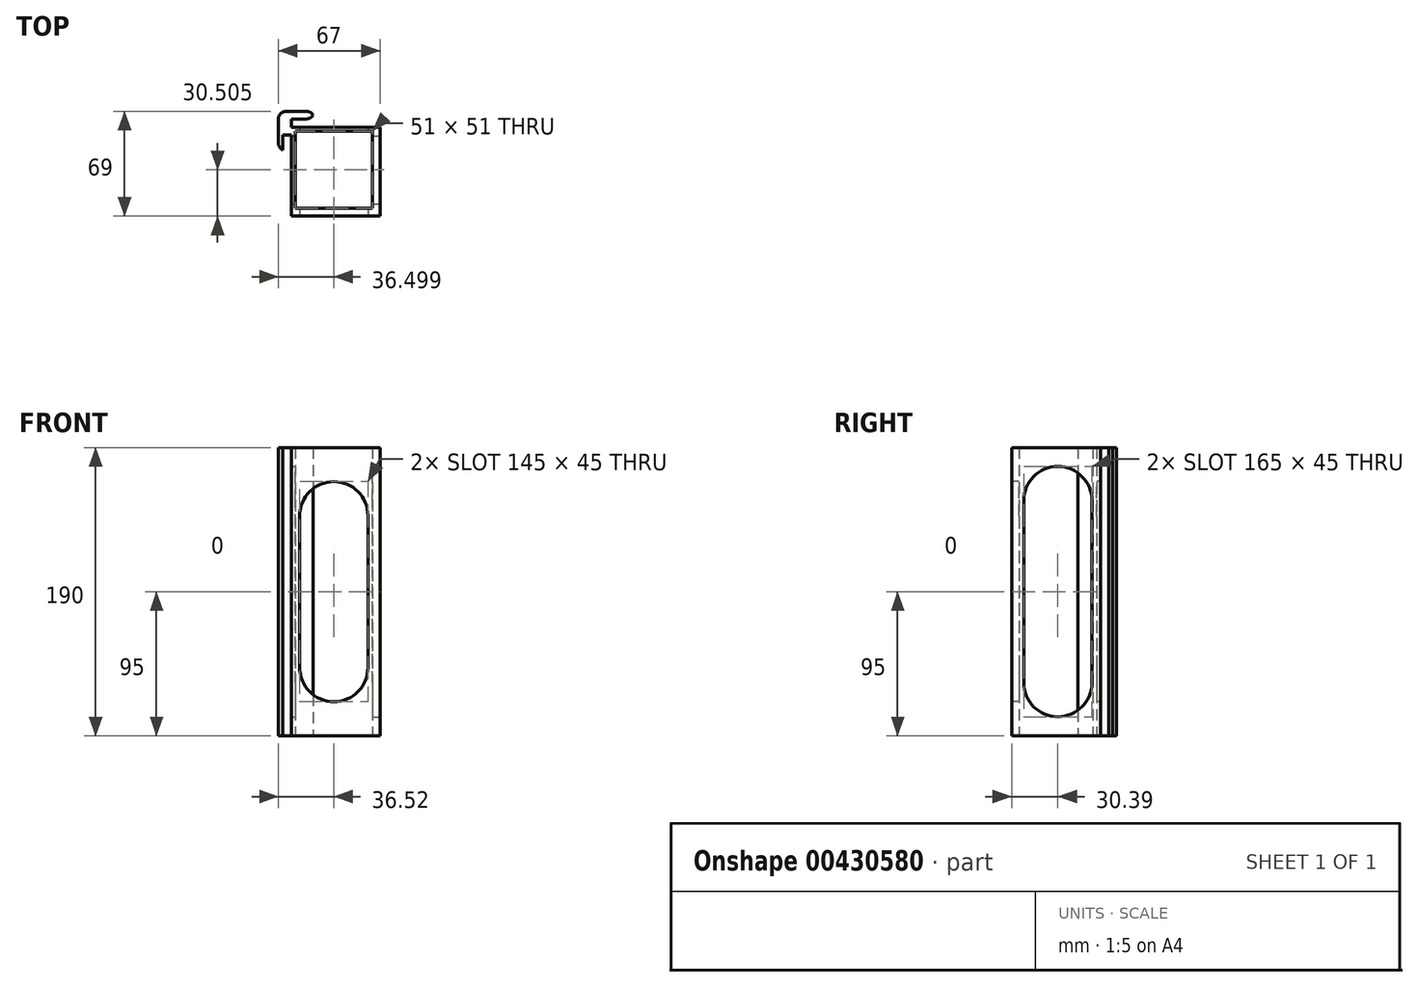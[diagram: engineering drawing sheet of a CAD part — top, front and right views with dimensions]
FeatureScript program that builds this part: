
annotation { "Feature Type Name" : "Feature", "Feature Type Description" : "" }
export const myFeature = defineFeature(function(context is Context, id is Id, definition is map)
    precondition{}
    {
        {
            var Q0;
            Q0=qCreatedBy(makeId("Top.planeOp"),FACE);
            var sketch = newSketch(context, id + "F0", { "sketchPlane" : qUnion([Q0])});
            skLineSegment(sketch, "E0.bottom", {"start": v(25.48, -25.39) * mm, "end": v(-25.52, -25.39) * mm});
            skLineSegment(sketch, "E0.top", {"start": v(25.48, 25.61) * mm, "end": v(-25.52, 25.61) * mm});
            skLineSegment(sketch, "E0.left", {"start": v(25.48, -25.39) * mm, "end": v(25.48, 25.61) * mm});
            skLineSegment(sketch, "E0.right", {"start": v(-25.52, -25.39) * mm, "end": v(-25.52, 25.61) * mm});
            skPoint(sketch, "E0.middle", {"position": v(-0.02, 0.11) * mm});
            skLineSegment(sketch, "E1.bottom", {"start": v(-28.02, 28.11) * mm, "end": v(30.48, 28.11) * mm});
            skLineSegment(sketch, "E1.top", {"start": v(-28.02, -30.39) * mm, "end": v(30.48, -30.39) * mm});
            skLineSegment(sketch, "E1.left", {"start": v(-28.02, 28.11) * mm, "end": v(-28.02, -30.39) * mm});
            skLineSegment(sketch, "E1.right", {"start": v(30.48, 28.11) * mm, "end": v(30.48, -30.39) * mm});
            skLineSegment(sketch, "E2.bottom", {"start": v(-28.02, 28.11) * mm, "end": v(-23.02, 28.11) * mm});
            skLineSegment(sketch, "E2.top", {"start": v(-28.02, 33.61) * mm, "end": v(-23.02, 33.61) * mm});
            skLineSegment(sketch, "E2.left", {"start": v(-28.02, 28.11) * mm, "end": v(-28.02, 33.61) * mm});
            skLineSegment(sketch, "E3.bottom", {"start": v(-28.02, 28.11) * mm, "end": v(-33.52, 28.11) * mm});
            skLineSegment(sketch, "E3.top", {"start": v(-28.02, 23.11) * mm, "end": v(-33.52, 23.11) * mm});
            skLineSegment(sketch, "E3.left", {"start": v(-28.02, 28.11) * mm, "end": v(-28.02, 23.11) * mm});
            skLineSegment(sketch, "E3.right", {"start": v(-33.52, 28.11) * mm, "end": v(-33.52, 23.11) * mm});
            skLineSegment(sketch, "E4.bottom", {"start": v(-33.52, 28.11) * mm, "end": v(-36.52, 28.11) * mm});
            skLineSegment(sketch, "E4.top", {"start": v(-33.52, 13.11) * mm, "end": v(-36.52, 13.11) * mm});
            skLineSegment(sketch, "E4.left", {"start": v(-33.52, 28.11) * mm, "end": v(-33.52, 13.11) * mm});
            skLineSegment(sketch, "E4.right", {"start": v(-36.52, 28.11) * mm, "end": v(-36.52, 13.11) * mm});
            skLineSegment(sketch, "E5.bottom", {"start": v(-28.02, 33.61) * mm, "end": v(-13.02, 33.61) * mm});
            skLineSegment(sketch, "E5.top", {"start": v(-28.02, 38.61) * mm, "end": v(-13.02, 38.61) * mm});
            skLineSegment(sketch, "E5.left", {"start": v(-28.02, 33.61) * mm, "end": v(-28.02, 38.61) * mm});
            skLineSegment(sketch, "E5.right", {"start": v(-13.02, 33.61) * mm, "end": v(-13.02, 38.61) * mm});
            skLineSegment(sketch, "E6.bottom", {"start": v(-28.02, 28.11) * mm, "end": v(-36.52, 28.11) * mm});
            skLineSegment(sketch, "E6.top", {"start": v(-28.02, 38.61) * mm, "end": v(-36.52, 38.61) * mm});
            skLineSegment(sketch, "E6.left", {"start": v(-28.02, 28.11) * mm, "end": v(-28.02, 38.61) * mm});
            skLineSegment(sketch, "E6.right", {"start": v(-36.52, 28.11) * mm, "end": v(-36.52, 38.61) * mm});
            skSolve(sketch);
        }
        {
            var Q0;
            {var subQ4=sQuery(id+"F0.wireOp",EDGE,"E6.top");Q0=makeQuery(id+"F0.imprint","IMPRINT",FACE,{"disambiguationData":[TD([[makeQuery(id+"F0.imprint","IMPRINT",EDGE,{"derivedFrom":subQ4}),1.0]])]});}
            var Q1;
            {var subQ4=sQuery(id+"F0.wireOp",EDGE,"E5.top");Q1=makeQuery(id+"F0.imprint","IMPRINT",FACE,{"disambiguationData":[TD([[makeQuery(id+"F0.imprint","IMPRINT",EDGE,{"derivedFrom":subQ4}),-1.0]])]});}
            var Q2;
            {var subQ0=sQuery(id+"F0.wireOp",EDGE,"E3.top");Q2=makeQuery(id+"F0.imprint","IMPRINT",FACE,{"disambiguationData":[TD([[makeQuery(id+"F0.imprint","IMPRINT",EDGE,{"derivedFrom":subQ0}),-1.0]])]});}
            var Q3;
            {var subQ3=sQuery(id+"F0.wireOp",EDGE,"E4.top");Q3=makeQuery(id+"F0.imprint","IMPRINT",FACE,{"disambiguationData":[TD([[makeQuery(id+"F0.imprint","IMPRINT",EDGE,{"derivedFrom":subQ3}),-1.0]])]});}
            var Q4;
            Q4=makeQuery(id+"F0.imprint","IMPRINT",FACE,{"disambiguationData":[TD([[makeQuery(id+"F0.imprint","IMPRINT",EDGE,{"derivedFrom":sQuery(id+"F0.wireOp",EDGE,"E0.bottom")}),1.0]])]});
            extrude(context, id + "F1", {"entities" : qUnion([Q0, Q1, Q2, Q3, Q4]), "depth" : 190 * mm, "offsetDistance" : 25 * mm});
        }
        {
            var Q0;
            Q0=makeQuery(id+"F1.opExtrude","SWEPT_EDGE",EDGE,{"disambiguationData":[OSD([sQuery(id+"F0.wireOp",EDGE,"E6.top"),sQuery(id+"F0.wireOp",EDGE,"E6.right")])]});
            var Q1;
            Q1=makeQuery(id+"F1.opExtrude","SWEPT_EDGE",EDGE,{"disambiguationData":[OSD([sQuery(id+"F0.wireOp",EDGE,"E5.top"),sQuery(id+"F0.wireOp",EDGE,"E5.right")])]});
            var Q2;
            Q2=makeQuery(id+"F1.opExtrude","SWEPT_EDGE",EDGE,{"disambiguationData":[OSD([sQuery(id+"F0.wireOp",EDGE,"E5.bottom"),sQuery(id+"F0.wireOp",EDGE,"E5.right")])]});
            var Q3;
            Q3=makeQuery(id+"F1.opExtrude","SWEPT_EDGE",EDGE,{"disambiguationData":[OSD([sQuery(id+"F0.wireOp",EDGE,"E4.top"),sQuery(id+"F0.wireOp",EDGE,"E4.right")])]});
            fillet(context, id + "F2", {"entities" : qUnion([Q0, Q1, Q2, Q3]), "tangentPropagation" : true, "radius" : 5 * mm, "defaultsChanged" : false, "vertexSettings" : [], "allowEdgeOverflow" : false});
        }
        {
            var Q0;
            Q0=makeQuery(id+"F1.opExtrude","SWEPT_FACE",FACE,{"disambiguationData":[OSD([sQuery(id+"F0.wireOp",EDGE,"E1.right")])]});
            var sketch = newSketch(context, id + "F3", { "sketchPlane" : qUnion([Q0])});
            skCircle(sketch, "E7", {"center": v(0, 35) * mm, "radius": 22.5 * mm});
            skCircle(sketch, "E8", {"center": v(0, 155) * mm, "radius": 22.5 * mm});
            skLineSegment(sketch, "E9.bottom", {"start": v(-22.5, 155) * mm, "end": v(22.5, 155) * mm});
            skLineSegment(sketch, "E9.top", {"start": v(-22.5, 35) * mm, "end": v(22.5, 35) * mm});
            skLineSegment(sketch, "E9.left", {"start": v(-22.5, 155) * mm, "end": v(-22.5, 35) * mm});
            skLineSegment(sketch, "E9.right", {"start": v(22.5, 155) * mm, "end": v(22.5, 35) * mm});
            skSolve(sketch);
        }
        {
            var Q0;
            {var subQ0=sQuery(id+"F3.wireOp",EDGE,"E9.bottom");Q0=makeQuery(id+"F3.imprint","IMPRINT",FACE,{"disambiguationData":[TD([[makeQuery(id+"F3.imprint","IMPRINT",EDGE,{"derivedFrom":subQ0}),1.0]])]});}
            var Q1;
            {var subQ0=sQuery(id+"F3.wireOp",EDGE,"E9.bottom");Q1=makeQuery(id+"F3.imprint","IMPRINT",FACE,{"disambiguationData":[TD([[makeQuery(id+"F3.imprint","IMPRINT",EDGE,{"derivedFrom":subQ0}),-1.0]])]});}
            var Q2;
            {var subQ0=sQuery(id+"F3.wireOp",EDGE,"E9.left");Q2=makeQuery(id+"F3.imprint","IMPRINT",FACE,{"disambiguationData":[TD([[makeQuery(id+"F3.imprint","IMPRINT",EDGE,{"derivedFrom":subQ0}),1.0]])]});}
            var Q3;
            {var subQ0=sQuery(id+"F3.wireOp",EDGE,"E9.top");Q3=makeQuery(id+"F3.imprint","IMPRINT",FACE,{"disambiguationData":[TD([[makeQuery(id+"F3.imprint","IMPRINT",EDGE,{"derivedFrom":subQ0}),1.0]])]});}
            var Q4;
            {var subQ0=sQuery(id+"F3.wireOp",EDGE,"E9.top");Q4=makeQuery(id+"F3.imprint","IMPRINT",FACE,{"disambiguationData":[TD([[makeQuery(id+"F3.imprint","IMPRINT",EDGE,{"derivedFrom":subQ0}),-1.0]])]});}
            extrude(context, id + "F4", {"entities" : qUnion([Q0, Q1, Q2, Q3, Q4]), "operationType" : NewBodyOperationType.REMOVE, "oppositeDirection" : true, "depth" : 60 * mm, "offsetDistance" : 25 * mm});
        }
        {
            var Q0;
            Q0=makeQuery(id+"F1.opExtrude","SWEPT_FACE",FACE,{"disambiguationData":[OSD([sQuery(id+"F0.wireOp",EDGE,"E1.top")])]});
            var sketch = newSketch(context, id + "F5", { "sketchPlane" : qUnion([Q0])});
            skCircle(sketch, "E10", {"center": v(0, 145) * mm, "radius": 22.5 * mm});
            skCircle(sketch, "E11", {"center": v(0, 45) * mm, "radius": 22.5 * mm});
            skLineSegment(sketch, "E12.bottom", {"start": v(-22.5, 145) * mm, "end": v(22.5, 145) * mm});
            skLineSegment(sketch, "E12.top", {"start": v(-22.5, 45) * mm, "end": v(22.5, 45) * mm});
            skLineSegment(sketch, "E12.left", {"start": v(-22.5, 145) * mm, "end": v(-22.5, 45) * mm});
            skLineSegment(sketch, "E12.right", {"start": v(22.5, 145) * mm, "end": v(22.5, 45) * mm});
            skSolve(sketch);
        }
        {
            var Q0;
            {var subQ0=sQuery(id+"F5.wireOp",EDGE,"E12.bottom");Q0=makeQuery(id+"F5.imprint","IMPRINT",FACE,{"disambiguationData":[TD([[makeQuery(id+"F5.imprint","IMPRINT",EDGE,{"derivedFrom":subQ0}),1.0]])]});}
            var Q1;
            {var subQ0=sQuery(id+"F5.wireOp",EDGE,"E12.bottom");Q1=makeQuery(id+"F5.imprint","IMPRINT",FACE,{"disambiguationData":[TD([[makeQuery(id+"F5.imprint","IMPRINT",EDGE,{"derivedFrom":subQ0}),-1.0]])]});}
            var Q2;
            {var subQ0=sQuery(id+"F5.wireOp",EDGE,"E12.left");Q2=makeQuery(id+"F5.imprint","IMPRINT",FACE,{"disambiguationData":[TD([[makeQuery(id+"F5.imprint","IMPRINT",EDGE,{"derivedFrom":subQ0}),1.0]])]});}
            var Q3;
            {var subQ0=sQuery(id+"F5.wireOp",EDGE,"E12.top");Q3=makeQuery(id+"F5.imprint","IMPRINT",FACE,{"disambiguationData":[TD([[makeQuery(id+"F5.imprint","IMPRINT",EDGE,{"derivedFrom":subQ0}),1.0]])]});}
            var Q4;
            {var subQ0=sQuery(id+"F5.wireOp",EDGE,"E12.top");Q4=makeQuery(id+"F5.imprint","IMPRINT",FACE,{"disambiguationData":[TD([[makeQuery(id+"F5.imprint","IMPRINT",EDGE,{"derivedFrom":subQ0}),-1.0]])]});}
            extrude(context, id + "F6", {"entities" : qUnion([Q0, Q1, Q2, Q3, Q4]), "operationType" : NewBodyOperationType.REMOVE, "oppositeDirection" : true, "depth" : 60 * mm, "offsetDistance" : 25 * mm});
        }
    });
